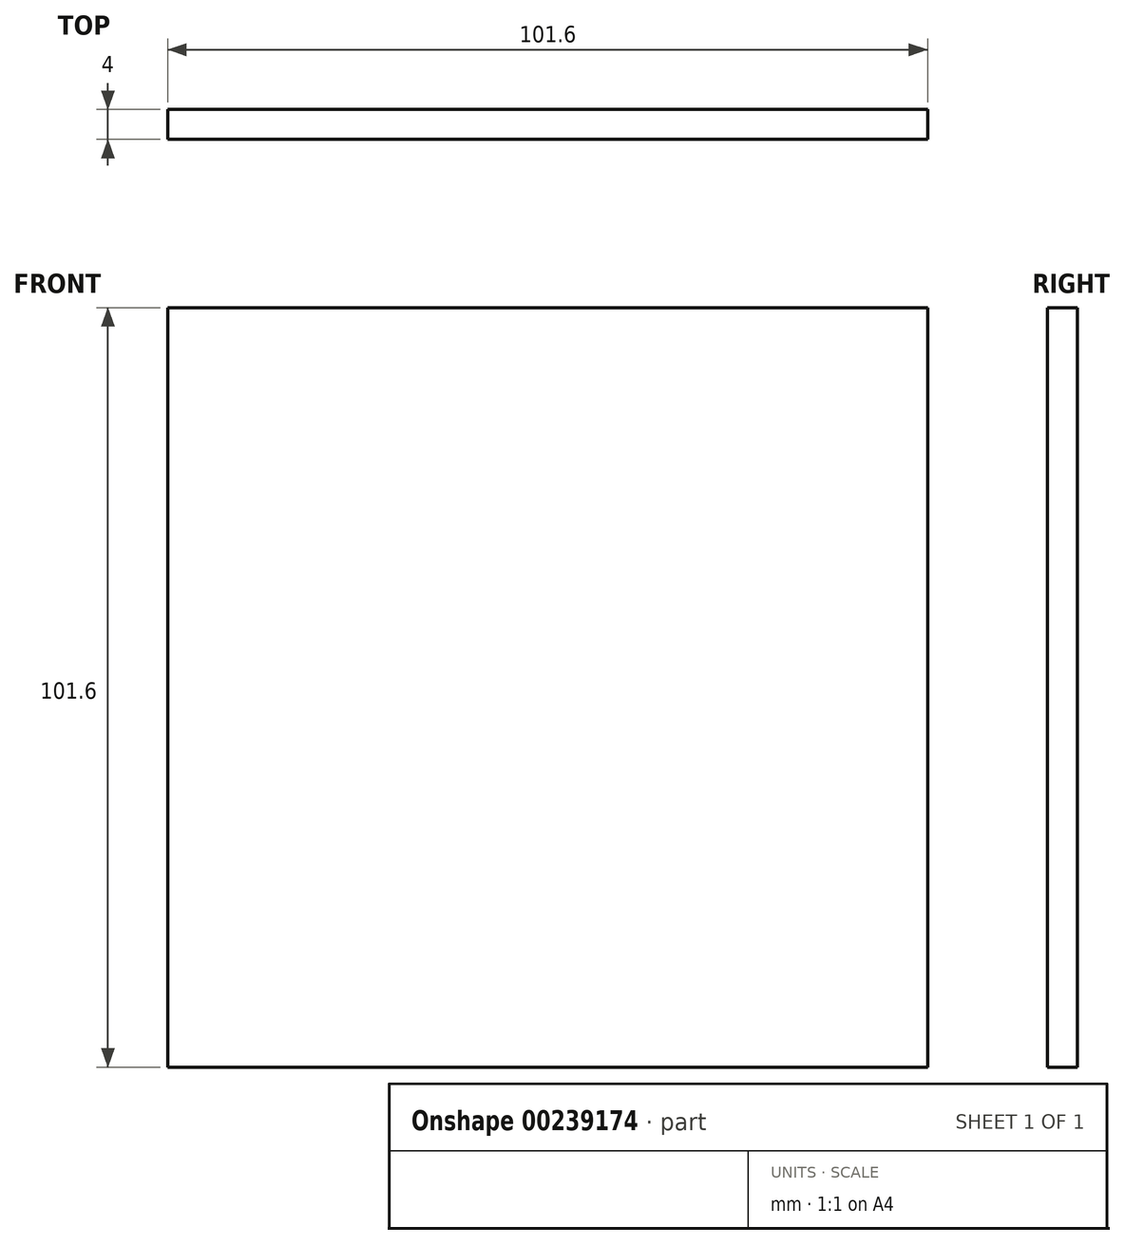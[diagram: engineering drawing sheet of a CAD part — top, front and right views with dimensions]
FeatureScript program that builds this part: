
annotation { "Feature Type Name" : "Feature", "Feature Type Description" : "" }
export const myFeature = defineFeature(function(context is Context, id is Id, definition is map)
    precondition{}
    {
        {
            assignVariable(context, id + "F0", {"name" : "L", "anyValue" : 4});
        }
        {
            var Q0;
            Q0=qCreatedBy(makeId("Front.planeOp"),FACE);
            var sketch = newSketch(context, id + "F1", { "sketchPlane" : qUnion([Q0])});
            skLineSegment(sketch, "E0.bottom", {"start": v(-49.4, 50.78) * mm, "end": v(52.2, 50.78) * mm});
            skLineSegment(sketch, "E0.top", {"start": v(-49.4, -50.82) * mm, "end": v(52.2, -50.82) * mm});
            skLineSegment(sketch, "E0.left", {"start": v(-49.4, 50.78) * mm, "end": v(-49.4, -50.82) * mm});
            skLineSegment(sketch, "E0.right", {"start": v(52.2, 50.78) * mm, "end": v(52.2, -50.82) * mm});
            skSolve(sketch);
        }
        {
            var Q0;
            Q0=makeQuery(id+"F1.imprint","IMPRINT",FACE,{"disambiguationData":[TD([[makeQuery(id+"F1.imprint","IMPRINT",EDGE,{"derivedFrom":sQuery(id+"F1.wireOp",EDGE,"E0.bottom")}),-1.0]])]});
            extrude(context, id + "F2", {"entities" : qUnion([Q0]), "endBound" : BoundingType.SYMMETRIC, "oppositeDirection" : true, "depth" : (getVariable(context, 'L')) * mm});
        }
    });
